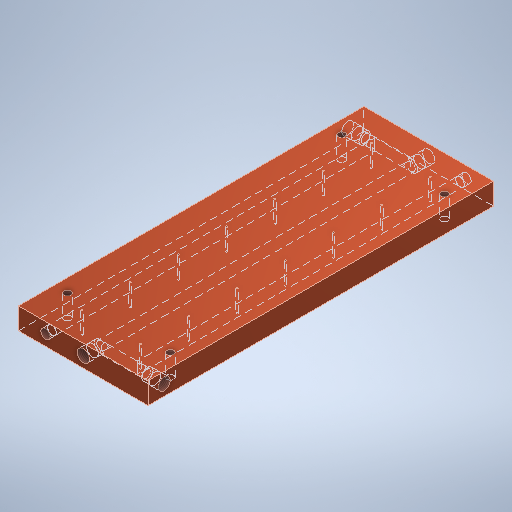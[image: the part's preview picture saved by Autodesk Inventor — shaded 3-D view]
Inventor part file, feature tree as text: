
AUTODESK INVENTOR PART (.ipt)
format: ipt  version: 2025 (Build 290162000, 162)  size: 377,344 bytes
history: native  units: mm
features: hole x13, other x6, sketch x4, extrude x1
ambient origin geometry x8: Origin, YZ Plane, XZ Plane, XY Plane, X Axis, Y Axis, Z Axis, Center Point
bodies: Solid1 (feature_tree)
feature tree (24):
  extrude  "Extrusion1"  Depth=320.0mm
  other  "Right Center Hole and Plug"
  hole  "Hole1"  [1 undecoded]
  other  "Back Hole and Plug"
  hole  "Hole2"  [1 undecoded]
  other  "Front Hole and Plug"
  hole  "Hole3"  [1 undecoded]
  other  "Left Inlet and threading"
  hole  "Left Inlet"  [1 undecoded]
  other  "Right Inlet and threading"
  hole  "Right Inlet"  [1 undecoded]
  hole  "Hole6"  [1 undecoded]
  hole  "Hole7"  [1 undecoded]
  hole  "Hole8"  [1 undecoded]
  hole  "Hole9"  [1 undecoded]
  hole  "Hole10"  [1 undecoded]
  hole  "Hole11"  [1 undecoded]
  hole  "Hole12"  [1 undecoded]
  hole  "Hole13"  [1 undecoded]
  sketch  "Sketch1"  dims[d0=120.0mm d1=320.0mm]
  other  "Left Center Hole and Plug"
  sketch  "Sketch8"  dims[d5=10.0mm]
  sketch  "Sketch9"  dims[d6=8.0mm d7=6.0mm d8=4.0mm d9=2.0mm d10=90.0deg d11=8.0mm d12=20.594885mm d13=10.0mm d14=15.0mm d15=10.7188mm d16=8.60806mm d17=4.0mm d18=2.0mm d19=90.0deg d20=15.664mm d21=20.594885mm d22=10.0mm d23=15.0mm d24=10.7188mm d25=8.60806mm d26=4.0mm d27=2.0mm d28=90.0deg d29=15.664mm d30=20.594885mm d31=10.0mm d32=25.0mm d33=8.0mm d34=6.0mm d35=4.0mm d36=2.0mm d37=90.0deg d38=305.0mm d39=20.594885mm d40=10.0mm d41=25.0mm d42=8.0mm d43=6.0mm d44=4.0mm d45=2.0mm d46=90.0deg d47=305.0mm d48=20.594885mm d49=0.624793mm d50=10.820654mm d51=0.624793mm d52=10.820654mm d53=8.0mm d54=8.608mm d55=4.0mm d56=2.0mm d57=90.0deg d58=60.0mm d59=20.594885mm d60=8.0mm d61=6.0mm d62=4.0mm d63=2.0mm d64=90.0deg d65=60.0mm d66=20.594885mm d67=10.7188mm d68=8.60806mm d69=0.624793mm d70=10.820654mm d71=4.0mm d72=2.0mm d73=90.0deg d74=15.664mm d75=20.594885mm d76=10.7188mm d77=8.608mm d78=0.624793mm d79=10.820654mm d80=4.0mm d81=2.0mm d82=90.0deg d83=15.664mm d84=20.594885mm d85=7.9502mm d86=5.98424mm d87=0.624793mm d88=8.363204mm d89=4.0mm d90=2.0mm d91=90.0deg d92=10.688mm d93=20.594885mm d94=7.9502mm d95=5.984mm d96=0.624793mm d97=8.363204mm d98=4.0mm d99=2.0mm d100=90.0deg d101=10.688mm d102=20.594885mm d103=33.0mm d104=12.4mm d105=12.4mm d106=33.0mm d107=6.647mm d108=16.0mm d109=4.0mm d110=2.0mm d111=90.0deg d112=8.0mm d113=20.594885mm d114=25.9mm d115=70.0mm d117=44.7mm d118=20.0mm d120=54.3mm d123=120.0mm d124=32.85mm d125=1.567mm d126=4.0mm d127=4.0mm d128=2.0mm d129=90.0deg d130=8.0mm d131=20.594885mm d132=254.0mm d133=95.2mm]
  sketch  "Sketch Rectangular Pattern1"  dims[d2=20.0mm d3=0.0mm d4=60.0mm]
note: 13 required parameter values undecoded (feature->parameter linkage not recoverable at this tier; creation-order binding heuristic only, values carry confidence <= 0.55)
